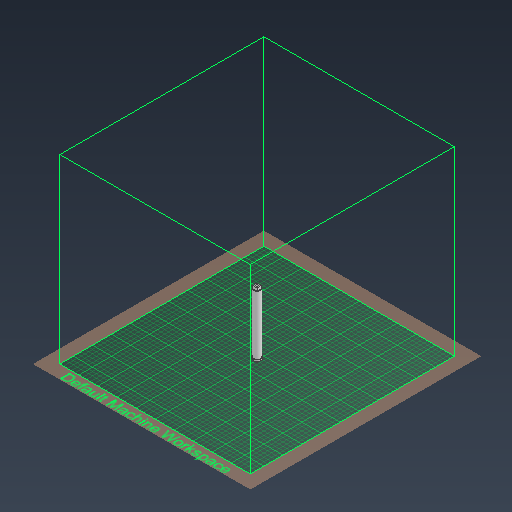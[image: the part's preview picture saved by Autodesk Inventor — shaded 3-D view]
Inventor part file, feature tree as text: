
AUTODESK INVENTOR PART (.ipt)
format: ipt  version: 2021 (Build 250183000, 183)  size: 275,456 bytes
history: native  units: mm
features: extrude x6, sketch x6
ambient origin geometry x8: Origin, YZ Plane, XZ Plane, XY Plane, X Axis, Y Axis, Z Axis, Center Point
bodies: Volumenkörper1 (feature_tree)
feature tree (12):
  extrude  "Extrusion1"  Depth=9.5mm
  extrude  "Extrusion2"  Depth=3.5mm
  extrude  "Extrusion3"  Depth=3.0mm
  extrude  "Extrusion4"  Depth=9.5mm
  extrude  "Extrusion5"  Depth=6.0mm
  extrude  "Extrusion6"  Depth=5.0mm
  sketch  "Skizze1"  dims[d0=9.5mm d1=9.5mm]
  sketch  "Skizze2"  dims[d2=3.5mm d3=0.0mm d4=17.0mm]
  sketch  "Skizze3"  dims[d5=3.0mm d6=0.0mm d7=14.8mm]
  sketch  "Skizze4"  dims[d8=130.0mm d9=0.0mm d10=9.5mm]
  sketch  "Skizze5"  dims[d11=6.0mm d12=0.0mm d13=4.5mm]
  sketch  "Skizze6"  dims[d14=5.0mm d15=0.0mm d16=4.5mm d17=5.0mm d18=0.0mm d19=1.1mm]
